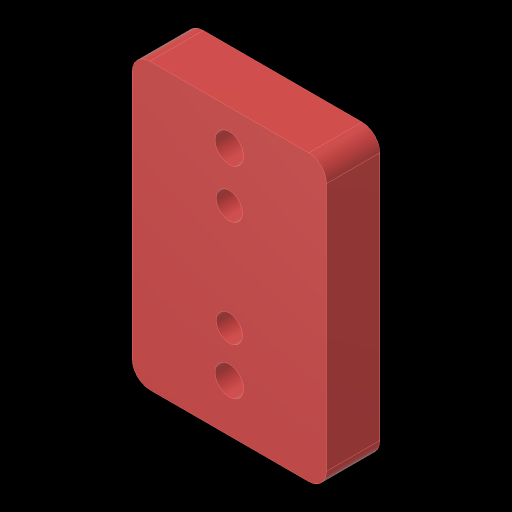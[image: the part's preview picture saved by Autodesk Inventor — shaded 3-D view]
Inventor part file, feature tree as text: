
AUTODESK INVENTOR PART (.ipt)
format: ipt  version: 2023.3 (Build 273359000, 359)  size: 134,144 bytes
history: native  units: in
note: dims shown in document units (in); Inventor stores cm internally (conversion verified against a paired STEP export)
features: hole x2, sketch x1, extrude x1, fillet x1
ambient origin geometry x8: Origin, YZ Plane, XZ Plane, XY Plane, X Axis, Y Axis, Z Axis, Center Point
bodies: Solid1 (feature_tree)
feature tree (5):
  sketch  "Sketch1"  dims[d0=1.3652in d1=2.0in d3=0.7447in d4=0.6in d6=0.375in d7=0.0in d8=0.201in d9=0.75in d10=0.375in d11=0.19in d12=0.5635in d13=1.0in d14=0.8108in d15=0.185in d16=0.75in d17=0.225in d18=0.25in d19=0.5635in d20=1.0in d21=0.8108in d22=0.125in d23=1.4142in d26=0.25in]
  extrude  "Extrusion1"  Depth=2.0in
  hole  "Hole1"  [1 undecoded]
  hole  "Hole2"  [1 undecoded]
  fillet  "Fillet1"  Radius=0.375in
note: 2 required parameter values undecoded (feature->parameter linkage not recoverable at this tier; creation-order binding heuristic only, values carry confidence <= 0.55)
